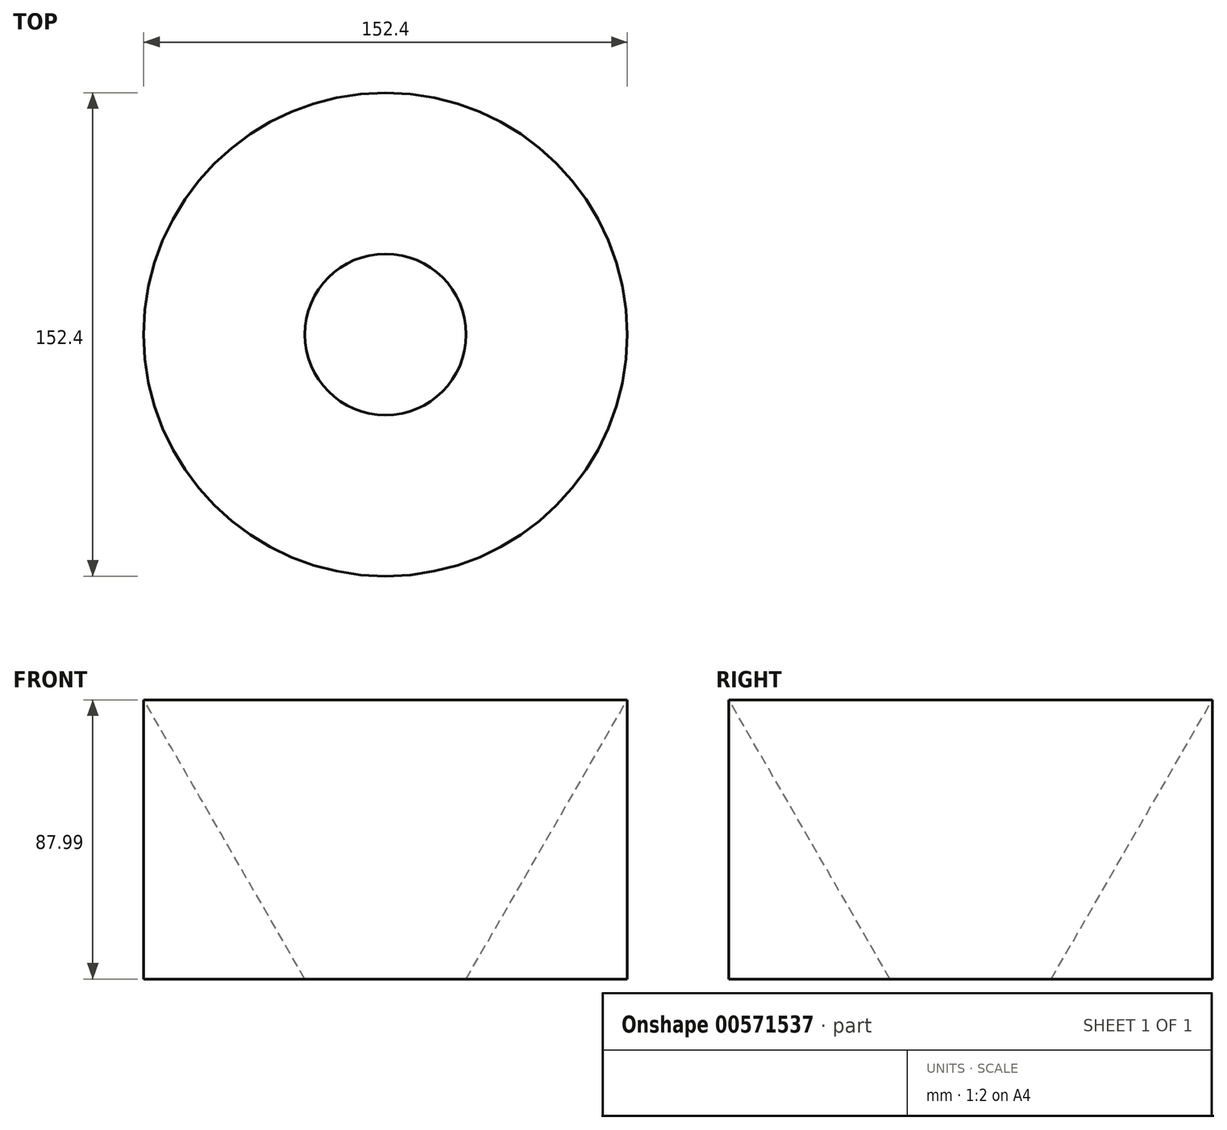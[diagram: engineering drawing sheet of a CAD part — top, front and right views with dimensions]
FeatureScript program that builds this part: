
annotation { "Feature Type Name" : "Feature", "Feature Type Description" : "" }
export const myFeature = defineFeature(function(context is Context, id is Id, definition is map)
    precondition{}
    {
        {
            var Q0;
            Q0=qCreatedBy(makeId("Front.planeOp"),FACE);
            var sketch = newSketch(context, id + "F0", { "sketchPlane" : qUnion([Q0])});
            skLineSegment(sketch, "E0", {"start": v(0, 0) * mm, "end": v(50.8, 0) * mm});
            skLineSegment(sketch, "E1", {"start": v(50.8, 0) * mm, "end": v(0, 87.99) * mm});
            skLineSegment(sketch, "E2", {"start": v(0, 87.99) * mm, "end": v(0, 0) * mm});
            skLineSegment(sketch, "E3", {"start": v(76.2, 18.86) * mm, "end": v(76.2, 42.91) * mm});
            skSolve(sketch);
        }
        {
            var Q0;
            Q0=makeQuery(id+"F0.imprint","IMPRINT",FACE,{"disambiguationData":[TD([[makeQuery(id+"F0.imprint","IMPRINT",EDGE,{"derivedFrom":sQuery(id+"F0.wireOp",EDGE,"E0")}),1.0]])]});
            var Q1;
            Q1=sQuery(id+"F0.wireOp",EDGE,"E2");
            var Q2;
            Q2=sQuery(id+"F0.wireOp",EDGE,"E3");
            revolve(context, id + "F1", {"entities" : qUnion([Q0]), "surfaceEntities" : qUnion([Q1]), "axis" : qUnion([Q2]), "revolveType" : RevolveType.FULL});
        }
    });
